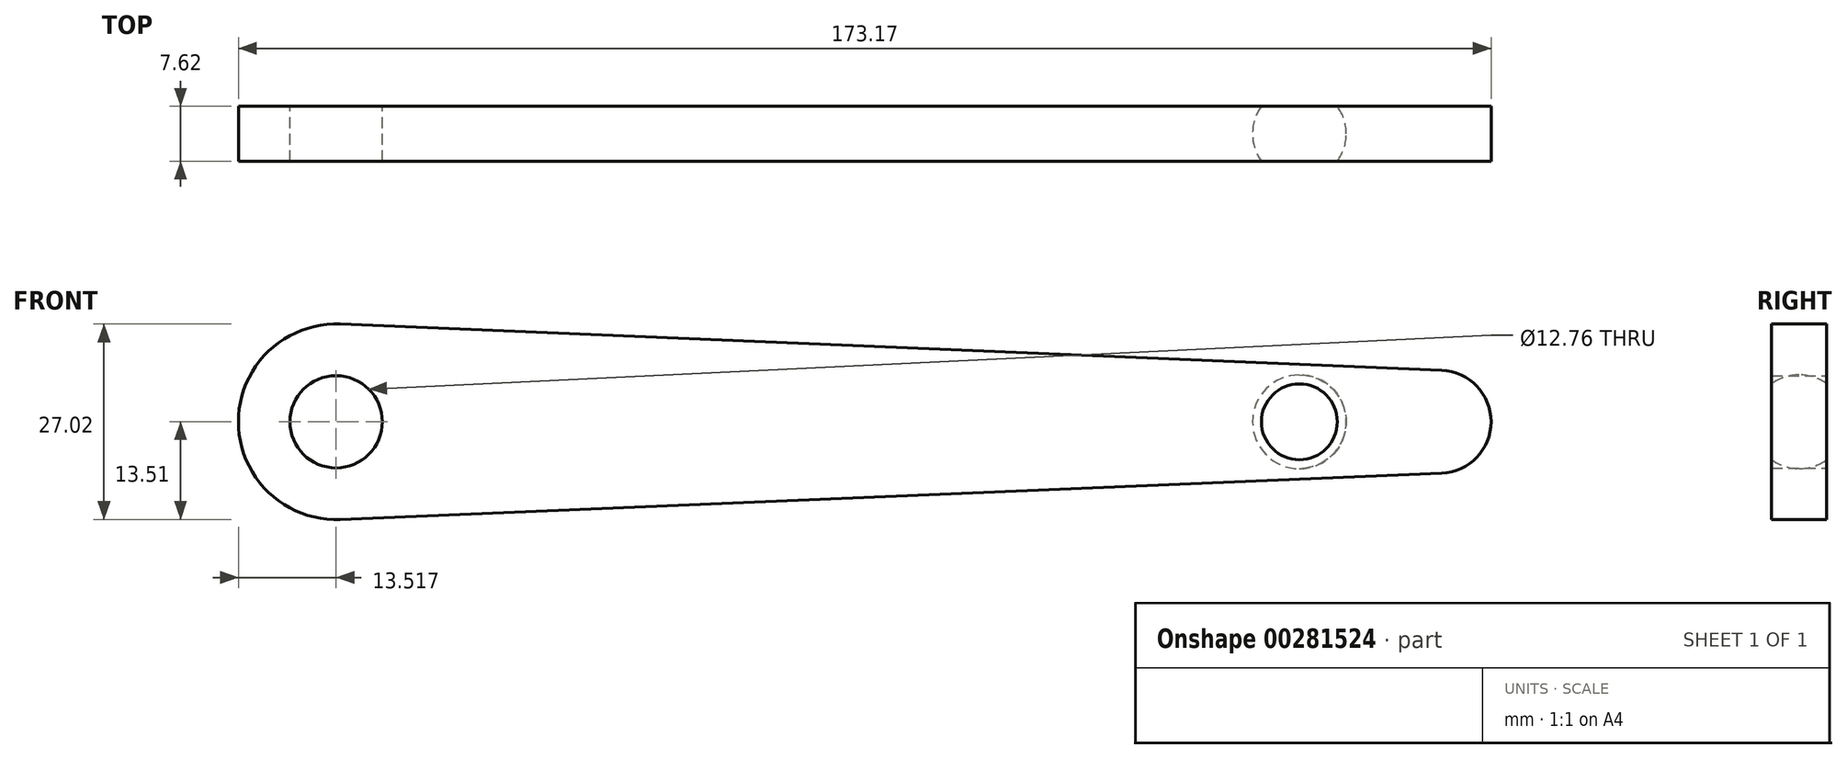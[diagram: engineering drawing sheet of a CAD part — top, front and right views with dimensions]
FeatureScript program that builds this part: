
annotation { "Feature Type Name" : "Feature", "Feature Type Description" : "" }
export const myFeature = defineFeature(function(context is Context, id is Id, definition is map)
    precondition{}
    {
        {
            var Q0;
            Q0=qCreatedBy(makeId("Front.planeOp"),FACE);
            var sketch = newSketch(context, id + "F0", { "sketchPlane" : qUnion([Q0])});
            skArc(sketch, "E0", {"start": v(-51.63, 13.5) * mm, "mid": v(-65.7, 0) * mm, "end": v(-51.63, -13.5) * mm});
            skCircle(sketch, "E1", {"center": v(-52.2, 0) * mm, "radius": 6.38 * mm});
            skArc(sketch, "E2", {"start": v(100.64, -7.12) * mm, "mid": v(107.46, 0) * mm, "end": v(100.64, 7.12) * mm});
            skLineSegment(sketch, "E3", {"start": v(-51.63, 13.5) * mm, "end": v(100.64, 7.12) * mm});
            skLineSegment(sketch, "E4", {"start": v(-51.63, -13.5) * mm, "end": v(100.64, -7.12) * mm});
            skSolve(sketch);
        }
        {
            var Q0;
            Q0=makeQuery(id+"F0.imprint","IMPRINT",FACE,{"disambiguationData":[TD([[makeQuery(id+"F0.imprint","IMPRINT",EDGE,{"derivedFrom":sQuery(id+"F0.wireOp",EDGE,"E0")}),1.0]])]});
            extrude(context, id + "F1", {"entities" : qUnion([Q0]), "endBound" : BoundingType.SYMMETRIC, "depth" : 7.62 * mm});
        }
        {
            var Q0;
            Q0=qCreatedBy(makeId("Front.planeOp"),FACE);
            var sketch = newSketch(context, id + "F2", { "sketchPlane" : qUnion([Q0])});
            skArc(sketch, "E5", {"start": v(80.96, 6.48) * mm, "mid": v(74.48, 0) * mm, "end": v(80.96, -6.48) * mm});
            skLineSegment(sketch, "E6", {"start": v(80.96, 6.48) * mm, "end": v(80.96, -6.48) * mm});
            skSolve(sketch);
        }
        {
            var Q0;
            Q0 = qSketchRegion(id + "F2", true);
            var Q1;
            Q1=sQuery(id+"F2.wireOp",EDGE,"E6");
            revolve(context, id + "F3", {"operationType" : NewBodyOperationType.REMOVE, "entities" : qUnion([Q0]), "axis" : qUnion([Q1]), "revolveType" : RevolveType.FULL, "oppositeDirection" : true});
        }
        {
            var Q0;
            Q0=qCreatedBy(makeId("Front.planeOp"),FACE);
            var sketch = newSketch(context, id + "F4", { "sketchPlane" : qUnion([Q0])});
            skCircle(sketch, "E7", {"center": v(80.96, 0) * mm, "radius": 3.77 * mm});
            skSolve(sketch);
        }
        {
            var Q0;
            Q0 = qSketchRegion(id + "F4", true);
            extrude(context, id + "F5", {"entities" : qUnion([Q0]), "operationType" : NewBodyOperationType.REMOVE, "endBound" : BoundingType.THROUGH_ALL, "oppositeDirection" : true, "depth" : 25.4 * mm, "hasSecondDirection" : true, "secondDirectionBound" : SecondDirectionBoundingType.THROUGH_ALL, "secondDirectionOppositeDirection" : false, "secondDirectionDepth" : 25.4 * mm});
        }
    });
